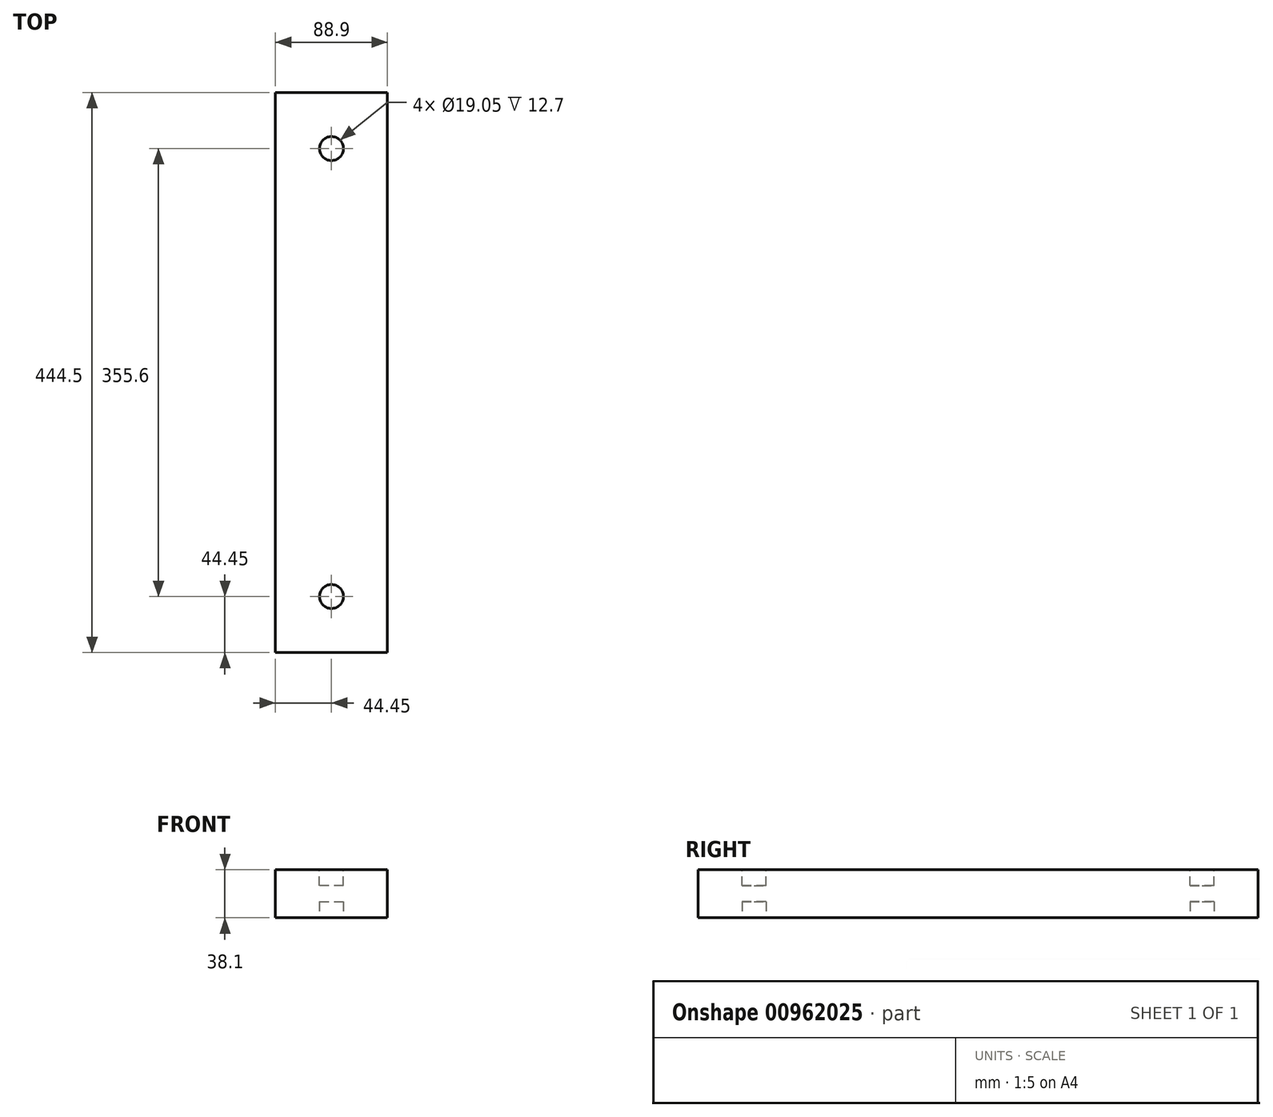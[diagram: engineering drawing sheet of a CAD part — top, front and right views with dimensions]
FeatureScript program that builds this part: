
annotation { "Feature Type Name" : "Feature", "Feature Type Description" : "" }
export const myFeature = defineFeature(function(context is Context, id is Id, definition is map)
    precondition{}
    {
        {
            var Q0;
            Q0=qCreatedBy(makeId("Front.planeOp"),FACE);
            var sketch = newSketch(context, id + "F0", { "sketchPlane" : qUnion([Q0])});
            skLineSegment(sketch, "E0.bottom", {"start": v(44.45, 19.05) * mm, "end": v(-44.45, 19.05) * mm});
            skLineSegment(sketch, "E0.top", {"start": v(44.45, -19.05) * mm, "end": v(-44.45, -19.05) * mm});
            skLineSegment(sketch, "E0.left", {"start": v(44.45, 19.05) * mm, "end": v(44.45, -19.05) * mm});
            skLineSegment(sketch, "E0.right", {"start": v(-44.45, 19.05) * mm, "end": v(-44.45, -19.05) * mm});
            skPoint(sketch, "E0.middle", {"position": v(0, 0) * mm});
            skSolve(sketch);
        }
        {
            var Q0;
            Q0 = qSketchRegion(id + "F0", true);
            extrude(context, id + "F1", {"entities" : qUnion([Q0]), "endBound" : BoundingType.SYMMETRIC, "depth" : 444.5 * mm, "offsetDistance" : 25.4 * mm});
        }
        {
            var Q0;
            Q0=makeQuery(id+"F1.opExtrude","SWEPT_FACE",FACE,{"disambiguationData":[OSD([sQuery(id+"F0.wireOp",EDGE,"E0.bottom")])]});
            var sketch = newSketch(context, id + "F2", { "sketchPlane" : qUnion([Q0])});
            skCircle(sketch, "E1", {"center": v(0, 177.8) * mm, "radius": 9.53 * mm});
            skCircle(sketch, "E2", {"center": v(0, -177.8) * mm, "radius": 9.53 * mm});
            skSolve(sketch);
        }
        {
            var Q0;
            Q0 = qSketchRegion(id + "F2", true);
            extrude(context, id + "F3", {"entities" : qUnion([Q0]), "operationType" : NewBodyOperationType.REMOVE, "oppositeDirection" : true, "depth" : 12.7 * mm, "offsetDistance" : 25.4 * mm});
        }
        {
            var Q0;
            Q0=makeQuery(id+"F1.opExtrude","SWEPT_FACE",FACE,{"disambiguationData":[OSD([sQuery(id+"F0.wireOp",EDGE,"E0.top")])]});
            var sketch = newSketch(context, id + "F4", { "sketchPlane" : qUnion([Q0])});
            skCircle(sketch, "E3", {"center": v(0, -177.8) * mm, "radius": 9.53 * mm});
            skCircle(sketch, "E4", {"center": v(0, 177.8) * mm, "radius": 9.53 * mm});
            skSolve(sketch);
        }
        {
            var Q0;
            Q0 = qSketchRegion(id + "F4", true);
            extrude(context, id + "F5", {"entities" : qUnion([Q0]), "operationType" : NewBodyOperationType.REMOVE, "oppositeDirection" : true, "depth" : 12.7 * mm, "offsetDistance" : 25.4 * mm});
        }
    });
